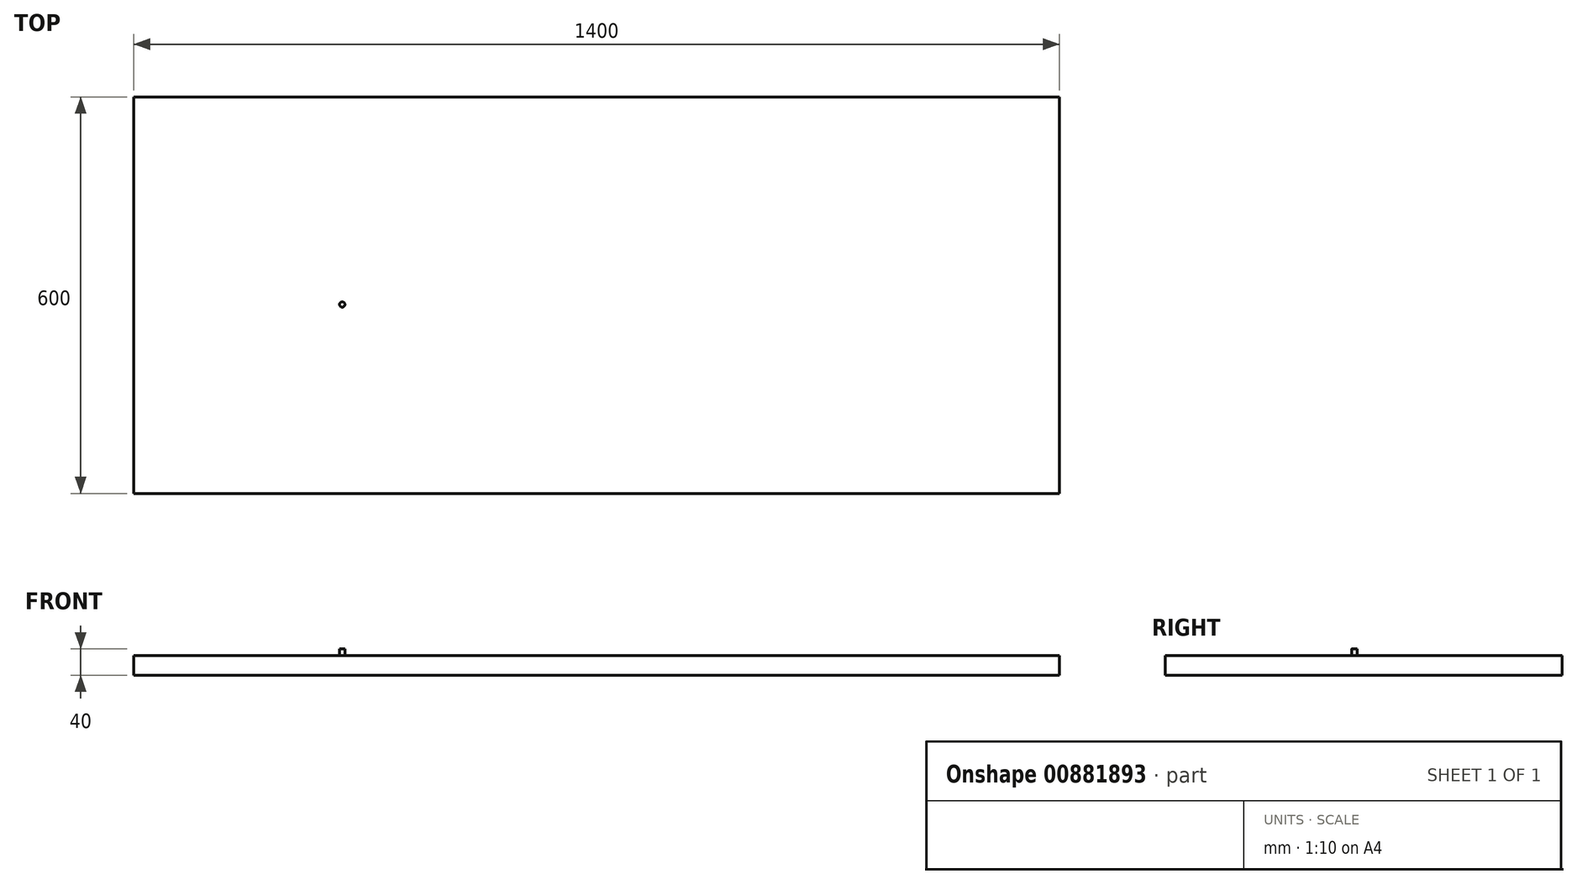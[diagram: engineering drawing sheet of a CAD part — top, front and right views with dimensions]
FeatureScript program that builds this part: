
annotation { "Feature Type Name" : "Feature", "Feature Type Description" : "" }
export const myFeature = defineFeature(function(context is Context, id is Id, definition is map)
    precondition{}
    {
        {
            var Q0;
            Q0=qCreatedBy(makeId("Top.planeOp"),FACE);
            var sketch = newSketch(context, id + "F0", { "sketchPlane" : qUnion([Q0])});
            skLineSegment(sketch, "E0.bottom", {"start": v(-700, 300) * mm, "end": v(700, 300) * mm});
            skLineSegment(sketch, "E0.top", {"start": v(-700, -300) * mm, "end": v(700, -300) * mm});
            skLineSegment(sketch, "E0.left", {"start": v(-700, 300) * mm, "end": v(-700, -300) * mm});
            skLineSegment(sketch, "E0.right", {"start": v(700, 300) * mm, "end": v(700, -300) * mm});
            skPoint(sketch, "E0.middle", {"position": v(0, 0) * mm});
            skSolve(sketch);
        }
        {
            var Q0;
            Q0=makeQuery(id+"F0.imprint","IMPRINT",FACE,{"disambiguationData":[TD([[makeQuery(id+"F0.imprint","IMPRINT",EDGE,{"derivedFrom":sQuery(id+"F0.wireOp",EDGE,"E0.bottom")}),-1.0]])]});
            extrude(context, id + "F1", {"entities" : qUnion([Q0]), "depth" : 30 * mm, "offsetDistance" : 25 * mm});
        }
        {
            var Q0;
            Q0=makeQuery(id+"F1.opExtrude","CAP_FACE",FACE,{"disambiguationData":[OSD([sQuery(id+"F0.wireOp",EDGE,"E0.bottom"),sQuery(id+"F0.wireOp",EDGE,"E0.top"),sQuery(id+"F0.wireOp",EDGE,"E0.left"),sQuery(id+"F0.wireOp",EDGE,"E0.right")])],"isStart":true});
            var sketch = newSketch(context, id + "F2", { "sketchPlane" : qUnion([Q0])});
            skPoint(sketch, "E1", {"position": v(650, 290) * mm});
            skPoint(sketch, "E2", {"position": v(400, 290) * mm});
            skSolve(sketch);
        }
        {
            var Q0;
            Q0=makeQuery(id+"F1.opExtrude","CAP_FACE",FACE,{"disambiguationData":[OSD([sQuery(id+"F0.wireOp",EDGE,"E0.bottom"),sQuery(id+"F0.wireOp",EDGE,"E0.top"),sQuery(id+"F0.wireOp",EDGE,"E0.left"),sQuery(id+"F0.wireOp",EDGE,"E0.right")])],"isStart":false});
            var sketch = newSketch(context, id + "F3", { "sketchPlane" : qUnion([Q0])});
            skCircle(sketch, "E3", {"center": v(-384.52, -13.97) * mm, "radius": 4 * mm});
            skSolve(sketch);
        }
        {
            var Q0;
            Q0 = qSketchRegion(id + "F3", true);
            extrude(context, id + "F4", {"entities" : qUnion([Q0]), "depth" : 10 * mm, "offsetDistance" : 25 * mm});
        }
    });
